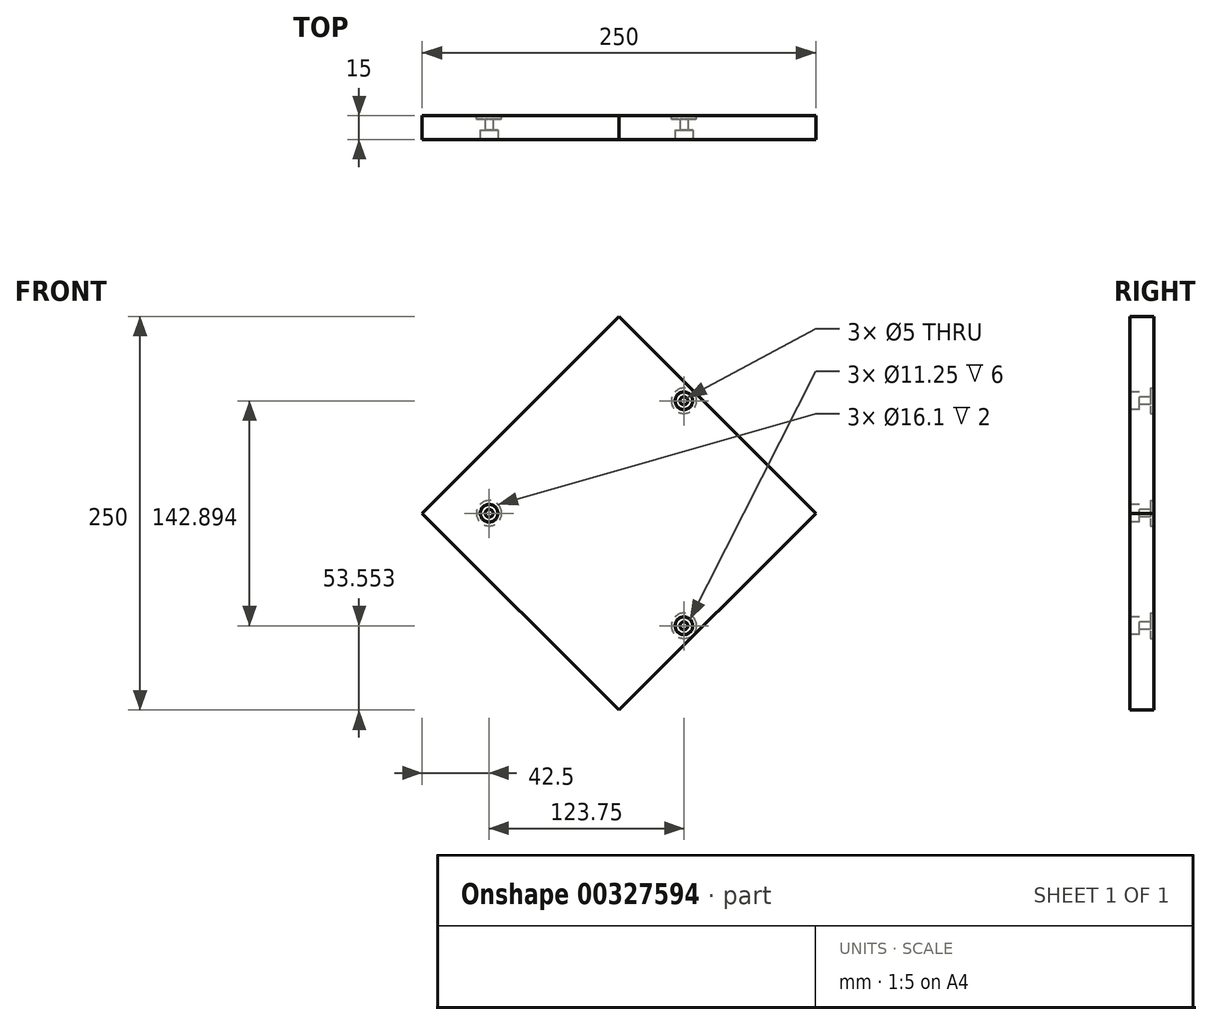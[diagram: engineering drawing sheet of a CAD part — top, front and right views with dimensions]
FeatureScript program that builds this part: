
annotation { "Feature Type Name" : "Feature", "Feature Type Description" : "" }
export const myFeature = defineFeature(function(context is Context, id is Id, definition is map)
    precondition{}
    {
        {
            var Q0;
            Q0=qCreatedBy(makeId("Front.planeOp"),FACE);
            var sketch = newSketch(context, id + "F0", { "sketchPlane" : qUnion([Q0])});
            skLineSegment(sketch, "E0", {"start": v(0, 111.82) * mm, "end": v(0, -93.68) * mm, "construction": true});
            skLineSegment(sketch, "E1", {"start": v(114.09, 0) * mm, "end": v(-79.4, 0) * mm, "construction": true});
            skLineSegment(sketch, "E2", {"start": v(0, 125) * mm, "end": v(-125, 0) * mm});
            skLineSegment(sketch, "E3", {"start": v(-125, 0) * mm, "end": v(0, -125) * mm});
            skLineSegment(sketch, "E4.MirrorCS", {"start": v(0, 125) * mm, "end": v(125, 0) * mm});
            skLineSegment(sketch, "E5.MirrorCS", {"start": v(125, 0) * mm, "end": v(0, -125) * mm});
            skSolve(sketch);
        }
        {
            var Q0;
            Q0 = qSketchRegion(id + "F0", true);
            extrude(context, id + "F1", {"entities" : qUnion([Q0]), "depth" : 15 * mm});
        }
        {
            var Q0;
            Q0=makeQuery(id+"F1.opExtrude","CAP_FACE",FACE,{"disambiguationData":[OSD([sQuery(id+"F0.wireOp",EDGE,"E2"),sQuery(id+"F0.wireOp",EDGE,"E3"),sQuery(id+"F0.wireOp",EDGE,"E4.MirrorCS"),sQuery(id+"F0.wireOp",EDGE,"E5.MirrorCS")])],"isStart":false});
            var sketch = newSketch(context, id + "F2", { "sketchPlane" : qUnion([Q0])});
            skLineSegment(sketch, "E6", {"start": v(-125, 0) * mm, "end": v(135.73, 0) * mm, "construction": true});
            skLineSegment(sketch, "E7", {"start": v(0, 125) * mm, "end": v(0, -142.51) * mm, "construction": true});
            skCircle(sketch, "E8", {"center": v(0, 0) * mm, "radius": 82.5 * mm, "construction": true});
            skLineSegment(sketch, "E9", {"start": v(0, 0) * mm, "end": v(61.34, -106.25) * mm, "construction": true});
            skLineSegment(sketch, "E10", {"start": v(0, 0) * mm, "end": v(59.96, 103.86) * mm, "construction": true});
            skPoint(sketch, "E11", {"position": v(-82.5, 0) * mm});
            skPoint(sketch, "E12", {"position": v(41.25, 71.45) * mm});
            skPoint(sketch, "E13", {"position": v(41.25, -71.45) * mm});
            skCircle(sketch, "E14", {"center": v(-82.5, 0) * mm, "radius": 8.05 * mm});
            skCircle(sketch, "E15", {"center": v(41.25, -71.45) * mm, "radius": 8.05 * mm});
            skCircle(sketch, "E16", {"center": v(41.25, 71.45) * mm, "radius": 8.05 * mm});
            skSolve(sketch);
        }
        {
            var Q0;
            Q0=sQuery(id+"F2.wireOp",VERTEX,"E11");
            var Q1;
            Q1=sQuery(id+"F2.wireOp",VERTEX,"E13");
            var Q2;
            Q2=sQuery(id+"F2.wireOp",VERTEX,"E12");
            var Q3;
            Q3=makeQuery(id+"F1.opExtrude","SWEPT_BODY",BODY,{"disambiguationData":[OSD([sQuery(id+"F0.wireOp",EDGE,"E2"),sQuery(id+"F0.wireOp",EDGE,"E3"),sQuery(id+"F0.wireOp",EDGE,"E4.MirrorCS"),sQuery(id+"F0.wireOp",EDGE,"E5.MirrorCS")])]});
            hole(context, id + "F3", {"style" : HoleStyle.C_BORE, "endStyle" : HoleEndStyle.THROUGH, "standardTappedOrClearance" : lookupTablePath({ "standard" : "ISO", "engagement" : "75%", "pitch" : "1 mm", "size" : "M6", "type" : "Tapped" }), "standardBlindInLast" : lookupTablePath({ "standard" : "ISO", "engagement" : "75%", "pitch" : "1 mm", "size" : "M6", "type" : "Tapped" }), "holeDiameter" : 5 * mm, "cBoreDiameter" : 11.25 * mm, "cBoreDepth" : 6 * mm, "showTappedDepth" : true, "tappedDepth" : 15 * mm, "tapClearance" : 1, "locations" : qUnion([Q0, Q1, Q2]), "scope" : qUnion([Q3]), "majorDiameter" : 6 * mm});
        }
        {
            var Q0;
            Q0=makeQuery(id+"F1.opExtrude","CAP_FACE",FACE,{"disambiguationData":[OSD([sQuery(id+"F0.wireOp",EDGE,"E2"),sQuery(id+"F0.wireOp",EDGE,"E3"),sQuery(id+"F0.wireOp",EDGE,"E4.MirrorCS"),sQuery(id+"F0.wireOp",EDGE,"E5.MirrorCS")])],"isStart":true});
            var sketch = newSketch(context, id + "F4", { "sketchPlane" : qUnion([Q0])});
            skCircle(sketch, "E17", {"center": v(82.5, 0) * mm, "radius": 8.05 * mm});
            skCircle(sketch, "E18", {"center": v(-41.25, -71.45) * mm, "radius": 8.05 * mm});
            skCircle(sketch, "E19", {"center": v(-41.25, 71.45) * mm, "radius": 8.05 * mm});
            skSolve(sketch);
        }
        {
            var Q0;
            Q0 = qSketchRegion(id + "F4", true);
            extrude(context, id + "F5", {"entities" : qUnion([Q0]), "operationType" : NewBodyOperationType.REMOVE, "oppositeDirection" : true, "depth" : 2 * mm});
        }
    });
